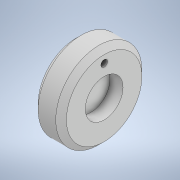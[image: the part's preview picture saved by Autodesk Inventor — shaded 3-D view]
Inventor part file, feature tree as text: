
AUTODESK INVENTOR PART (.ipt)
format: ipt  version: 2022 (Build 260153000, 153)  size: 129,536 bytes
history: native  units: mm
features: sketch x3, revolve x2, other x1, extrude x1
ambient origin geometry x8: Origin, YZ Plane, XZ Plane, XY Plane, X Axis, Y Axis, Z Axis, Center Point
bodies: Body1 (feature_tree)
feature tree (7):
  other  "Твердое тело1"
  revolve  "Вращение1"
  extrude  "Выдавливание1"  Depth=20.0mm
  revolve  "Вращение2"
  sketch  "Эскиз1"
  sketch  "Эскиз2"
  sketch  "Эскиз3"
